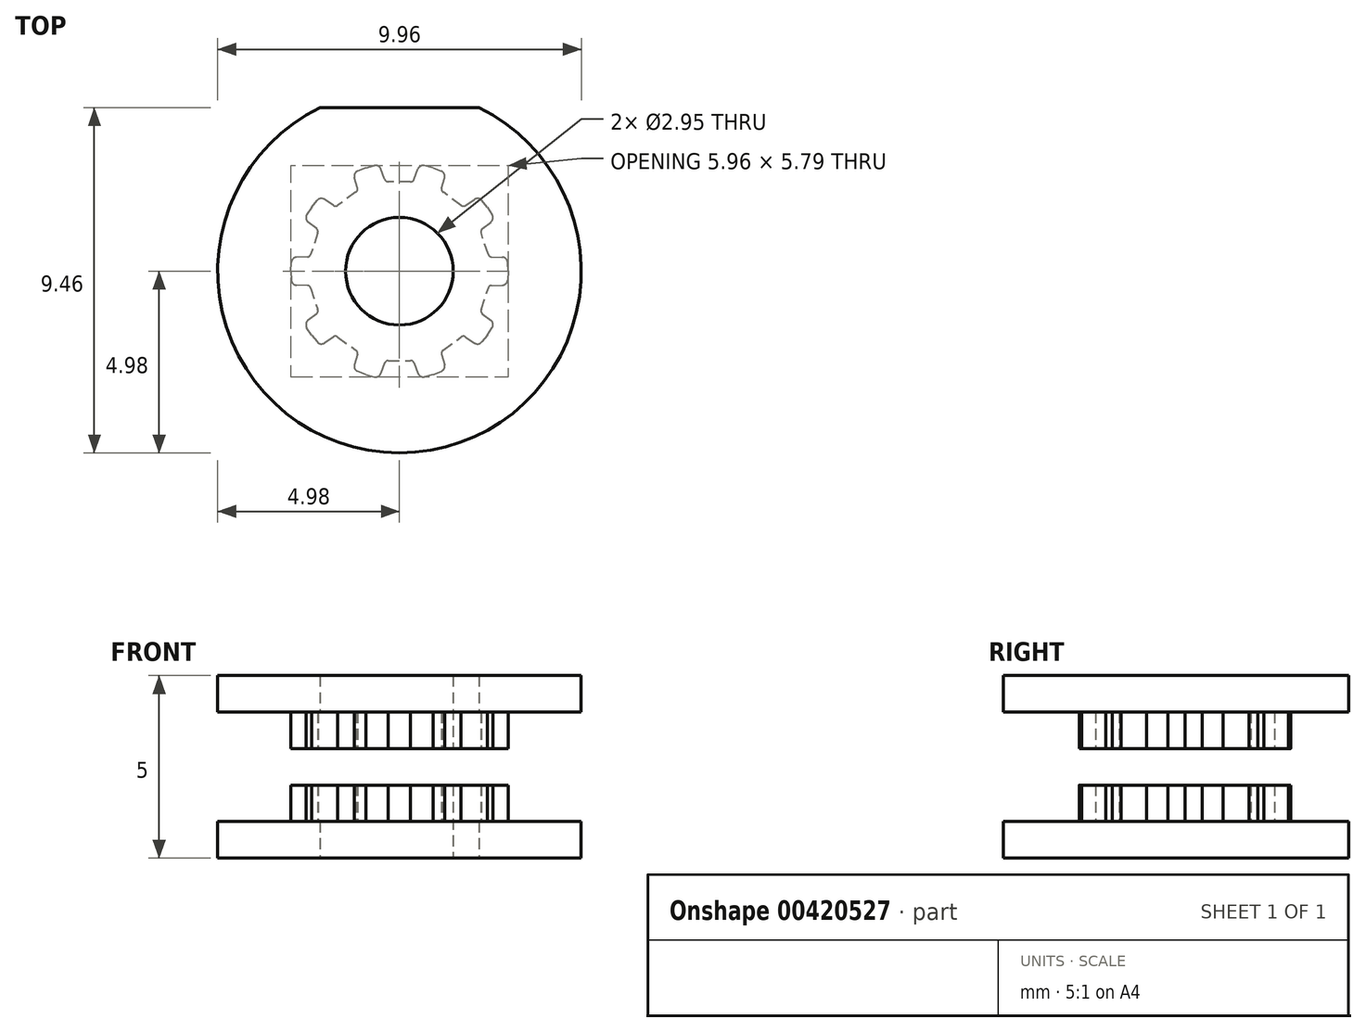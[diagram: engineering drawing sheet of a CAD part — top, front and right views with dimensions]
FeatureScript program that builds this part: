
annotation { "Feature Type Name" : "Feature", "Feature Type Description" : "" }
export const myFeature = defineFeature(function(context is Context, id is Id, definition is map)
    precondition{}
    {
        {
            assignVariable(context, id + "F0", {"name" : "teeth", "anyValue" : 10});
        }
        {
            var Q0;
            Q0=qCreatedBy(makeId("Top.planeOp"),FACE);
            var sketch = newSketch(context, id + "F1", { "sketchPlane" : qUnion([Q0])});
            skCircle(sketch, "E0", {"center": v(0, 0) * mm, "radius": 2.98 * mm, "construction": true});
            skLineSegment(sketch, "E1", {"start": v(0, 0) * mm, "end": v(0, 2.98) * mm, "construction": true});
            skLineSegment(sketch, "E2", {"start": v(0, 0) * mm, "end": v(0.92, 2.83) * mm, "construction": true});
            skArc(sketch, "E3", {"start": v(0.77, 2.36) * mm, "mid": v(0.39, 2.45) * mm, "end": v(0, 2.48) * mm, "construction": true});
            skArc(sketch, "E4", {"start": v(0.92, 2.83) * mm, "mid": v(0, 2.98) * mm, "end": v(-0.92, 2.83) * mm});
            skLineSegment(sketch, "E5", {"start": v(-0.92, 2.83) * mm, "end": v(-2.16, 6.64) * mm});
            skArc(sketch, "E6", {"start": v(2.16, 6.64) * mm, "mid": v(0, 6.98) * mm, "end": v(-2.16, 6.64) * mm});
            skLineSegment(sketch, "E7", {"start": v(2.16, 6.64) * mm, "end": v(0.92, 2.83) * mm});
            skPoint(sketch, "E8", {"position": v(0.38, 2.45) * mm});
            skLineSegment(sketch, "E9", {"start": v(0.4, 2.52) * mm, "end": v(0.5, 2.8) * mm});
            skLineSegment(sketch, "E10", {"start": v(0.92, 2.83) * mm, "end": v(0.69, 2.9) * mm});
            skPoint(sketch, "E11.visualSharp", {"position": v(0.55, 2.93) * mm});
            skArc(sketch, "E11.filletArc", {"start": v(0.69, 2.9) * mm, "mid": v(0.58, 2.88) * mm, "end": v(0.5, 2.8) * mm});
            skArc(sketch, "E12.filletArc", {"start": v(0.3, 2.45) * mm, "mid": v(0.37, 2.47) * mm, "end": v(0.4, 2.52) * mm});
            skLineSegment(sketch, "E13.MirrorCS", {"start": v(-0.4, 2.52) * mm, "end": v(-0.5, 2.8) * mm});
            skArc(sketch, "E14.MirrorCS", {"start": v(-0.3, 2.45) * mm, "mid": v(-0.37, 2.47) * mm, "end": v(-0.4, 2.52) * mm});
            skLineSegment(sketch, "E15.MirrorCS", {"start": v(0, 2.48) * mm, "end": v(-0.3, 2.45) * mm, "construction": true});
            skArc(sketch, "E16.MirrorCS", {"start": v(-0.69, 2.9) * mm, "mid": v(-0.58, 2.88) * mm, "end": v(-0.5, 2.8) * mm});
            skLineSegment(sketch, "E17.MirrorCS", {"start": v(-0.92, 2.83) * mm, "end": v(-0.69, 2.9) * mm});
            skLineSegment(sketch, "E18", {"start": v(0.3, 2.45) * mm, "end": v(-0.3, 2.45) * mm});
            skSolve(sketch);
        }
        {
            var Q0;
            Q0=qCreatedBy(makeId("Top.planeOp"),FACE);
            var sketch = newSketch(context, id + "F2", { "sketchPlane" : qUnion([Q0])});
            skCircle(sketch, "E19", {"center": v(0, 0) * mm, "radius": 4.98 * mm});
            skCircle(sketch, "E20", {"center": v(0, 0) * mm, "radius": 1.48 * mm});
            skLineSegment(sketch, "E21", {"start": v(-1.45, 0.27) * mm, "end": v(-1.45, -0.27) * mm, "construction": true});
            skLineSegment(sketch, "E22", {"start": v(1.45, 0.27) * mm, "end": v(1.45, -0.27) * mm, "construction": true});
            skCircle(sketch, "E23", {"center": v(-3.48, 0) * mm, "radius": 0.5 * mm, "construction": true});
            skCircle(sketch, "E24", {"center": v(3.48, 0) * mm, "radius": 0.5 * mm, "construction": true});
            skLineSegment(sketch, "E25", {"start": v(-3.48, 0) * mm, "end": v(3.48, 0) * mm, "construction": true});
            skLineSegment(sketch, "E26", {"start": v(-2.17, 4.48) * mm, "end": v(2.17, 4.48) * mm});
            skSolve(sketch);
        }
        {
            var Q0;
            Q0=makeQuery(id+"F2.imprint","IMPRINT",FACE,{"disambiguationData":[TD([[makeQuery(id+"F2.imprint","IMPRINT",EDGE,{"derivedFrom":sQuery(id+"F2.wireOp",EDGE,"E23")}),-1.0]])]});
            var Q1;
            {var subQ7=sQuery(id+"F2.wireOp",EDGE,"E26");Q1=makeQuery(id+"F2.imprint","IMPRINT",FACE,{"disambiguationData":[TD([[makeQuery(id+"F2.imprint","IMPRINT",EDGE,{"derivedFrom":subQ7}),-1.0]])]});}
            extrude(context, id + "F3", {"entities" : qUnion([Q0, Q1]), "depth" : 2.5 * mm, "offsetDistance" : 25 * mm});
        }
        {
            var Q0;
            {var subQ7=sQuery(id+"F2.wireOp",EDGE,"E26");Q0=makeQuery(id+"F2.imprint","IMPRINT",FACE,{"disambiguationData":[TD([[makeQuery(id+"F2.imprint","IMPRINT",EDGE,{"derivedFrom":subQ7}),-1.0]])]});}
            var Q1;
            {var subQ0=sQuery(id+"F2.wireOp",EDGE,"E21");Q1=makeQuery(id+"F2.imprint","IMPRINT",FACE,{"disambiguationData":[TD([[makeQuery(id+"F2.imprint","IMPRINT",EDGE,{"derivedFrom":subQ0}),-1.0]])]});}
            var Q2;
            {var subQ0=sQuery(id+"F2.wireOp",EDGE,"E22");Q2=makeQuery(id+"F2.imprint","IMPRINT",FACE,{"disambiguationData":[TD([[makeQuery(id+"F2.imprint","IMPRINT",EDGE,{"derivedFrom":subQ0}),1.0]])]});}
            extrude(context, id + "F4", {"entities" : qUnion([Q0, Q1, Q2]), "operationType" : NewBodyOperationType.ADD, "oppositeDirection" : true, "depth" : 2.5 * mm, "offsetDistance" : 25 * mm});
        }
        {
            var Q0;
            Q0=qSketchRegion(id+"F1",true);
            extrude(context, id + "F5", {"entities" : qUnion([Q0]), "endBound" : BoundingType.SYMMETRIC, "depth" : 3 * mm, "offsetDistance" : 25 * mm});
        }
        {
            var Q0;
            Q0=makeQuery(id+"F5.opExtrude","SWEPT_BODY",BODY,{"disambiguationData":[OSD([sQuery(id+"F1.wireOp",EDGE,"E5"),sQuery(id+"F1.wireOp",EDGE,"E6"),sQuery(id+"F1.wireOp",EDGE,"E7"),sQuery(id+"F1.wireOp",EDGE,"KHEIsP2H-6thQ-GgGZ-kpll-Wur77x7NuSWl"),sQuery(id+"F1.wireOp",EDGE,"E9"),sQuery(id+"F1.wireOp",EDGE,"E10"),sQuery(id+"F1.wireOp",EDGE,"E11.filletArc"),sQuery(id+"F1.wireOp",EDGE,"E12.filletArc"),sQuery(id+"F1.wireOp",EDGE,"E13.MirrorCS"),sQuery(id+"F1.wireOp",EDGE,"E14.MirrorCS"),sQuery(id+"F1.wireOp",EDGE,"E15.MirrorCS"),sQuery(id+"F1.wireOp",EDGE,"E16.MirrorCS"),sQuery(id+"F1.wireOp",EDGE,"E17.MirrorCS")])]});
            var Q1;
            Q1=sQuery(id+"F1.wireOp",EDGE,"E0");
            circularPattern(context, id + "F6", {"operationType" : NewBodyOperationType.REMOVE, "entities" : qUnion([Q0]), "axis" : qUnion([Q1]), "angle" : 360 * degree, "instanceCount" : getVariable(context, 'teeth'), "equalSpace" : true});
        }
        {
            var Q0;
            Q0=qSketchRegion(id+"F2",true);
            var Q1;
            {var subQ0=sQuery(id+"F2.wireOp",EDGE,"E22");Q1=makeQuery(id+"F2.imprint","IMPRINT",FACE,{"disambiguationData":[TD([[makeQuery(id+"F2.imprint","IMPRINT",EDGE,{"derivedFrom":subQ0}),1.0]])]});}
            var Q2;
            {var subQ0=sQuery(id+"F2.wireOp",EDGE,"E21");Q2=makeQuery(id+"F2.imprint","IMPRINT",FACE,{"disambiguationData":[TD([[makeQuery(id+"F2.imprint","IMPRINT",EDGE,{"derivedFrom":subQ0}),1.0]])]});}
            var Q3;
            {var subQ0=sQuery(id+"F2.wireOp",EDGE,"E21");Q3=makeQuery(id+"F2.imprint","IMPRINT",FACE,{"disambiguationData":[TD([[makeQuery(id+"F2.imprint","IMPRINT",EDGE,{"derivedFrom":subQ0}),-1.0]])]});}
            extrude(context, id + "F7", {"entities" : qUnion([Q0, Q1, Q2, Q3]), "operationType" : NewBodyOperationType.REMOVE, "endBound" : BoundingType.SYMMETRIC, "oppositeDirection" : true, "depth" : 1 * mm, "offsetDistance" : 25 * mm});
        }
        {
            var Q0;
            Q0=makeQuery(id+"F7.boolean.opBoolean","SPLIT",BODY,{"disambiguationData":[OD(0.0)],"derivedFrom":makeQuery(id+"F3.opExtrude","SWEPT_BODY",BODY,{"disambiguationData":[OSD([sQuery(id+"F2.wireOp",EDGE,"E19"),sQuery(id+"F2.wireOp",EDGE,"E20"),sQuery(id+"F2.wireOp",EDGE,"E21"),sQuery(id+"F2.wireOp",EDGE,"E22")])]})});
            transform(context, id + "F8", {"entities" : qUnion([Q0]), "transformType" : TransformType.TRANSLATION_3D, "dx" : 0 * mm, "dy" : 0 * mm, "dz" : -10 * mm, "makeCopy" : false});
        }
    });
